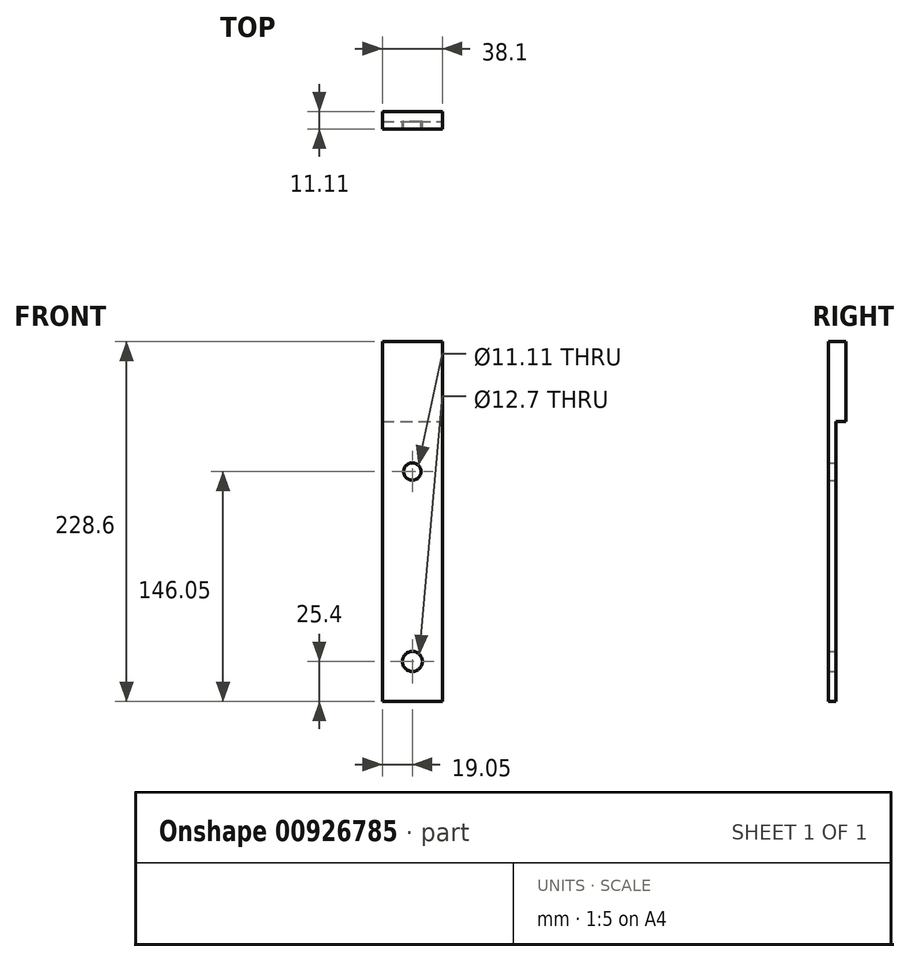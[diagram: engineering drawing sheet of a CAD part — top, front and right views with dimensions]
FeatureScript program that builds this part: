
annotation { "Feature Type Name" : "Feature", "Feature Type Description" : "" }
export const myFeature = defineFeature(function(context is Context, id is Id, definition is map)
    precondition{}
    {
        {
            var Q0;
            Q0=qCreatedBy(makeId("Front.planeOp"),FACE);
            var sketch = newSketch(context, id + "F0", { "sketchPlane" : qUnion([Q0])});
            skLineSegment(sketch, "E0.bottom", {"start": v(0, 0) * mm, "end": v(38.1, 0) * mm});
            skLineSegment(sketch, "E0.top", {"start": v(0, -228.6) * mm, "end": v(38.1, -228.6) * mm});
            skLineSegment(sketch, "E0.left", {"start": v(0, 0) * mm, "end": v(0, -228.6) * mm});
            skLineSegment(sketch, "E0.right", {"start": v(38.1, 0) * mm, "end": v(38.1, -228.6) * mm});
            skCircle(sketch, "E1", {"center": v(19.05, -82.55) * mm, "radius": 5.56 * mm});
            skPoint(sketch, "E1.centerSnap0", {"position": v(19.05, 0) * mm});
            skCircle(sketch, "E2", {"center": v(19.05, -203.2) * mm, "radius": 6.35 * mm});
            skSolve(sketch);
        }
        {
            var Q0;
            Q0=makeQuery(id+"F0.imprint","IMPRINT",FACE,{"disambiguationData":[TD([[makeQuery(id+"F0.imprint","IMPRINT",EDGE,{"derivedFrom":sQuery(id+"F0.wireOp",EDGE,"E0.bottom")}),-1.0]])]});
            extrude(context, id + "F1", {"entities" : qUnion([Q0]), "depth" : 4.76 * mm, "offsetDistance" : 25.4 * mm});
        }
        {
            var Q0;
            Q0=makeQuery(id+"F1.opExtrude","CAP_FACE",FACE,{"disambiguationData":[OSD([sQuery(id+"F0.wireOp",EDGE,"E0.bottom"),sQuery(id+"F0.wireOp",EDGE,"E0.top"),sQuery(id+"F0.wireOp",EDGE,"E0.left"),sQuery(id+"F0.wireOp",EDGE,"E0.right"),sQuery(id+"F0.wireOp",EDGE,"E1")])],"isStart":true});
            var sketch = newSketch(context, id + "F2", { "sketchPlane" : qUnion([Q0])});
            skLineSegment(sketch, "E3.bottom", {"start": v(0, 0) * mm, "end": v(-38.1, 0) * mm});
            skLineSegment(sketch, "E3.top", {"start": v(0, -50.8) * mm, "end": v(-38.1, -50.8) * mm});
            skLineSegment(sketch, "E3.left", {"start": v(0, 0) * mm, "end": v(0, -50.8) * mm});
            skLineSegment(sketch, "E3.right", {"start": v(-38.1, 0) * mm, "end": v(-38.1, -50.8) * mm});
            skSolve(sketch);
        }
        {
            var Q0;
            Q0=makeQuery(id+"F2.imprint","IMPRINT",FACE,{"disambiguationData":[TD([[makeQuery(id+"F2.imprint","IMPRINT",EDGE,{"derivedFrom":sQuery(id+"F2.wireOp",EDGE,"E3.bottom")}),1.0]])]});
            extrude(context, id + "F3", {"entities" : qUnion([Q0]), "operationType" : NewBodyOperationType.ADD, "depth" : 6.35 * mm, "offsetDistance" : 25.4 * mm});
        }
    });
